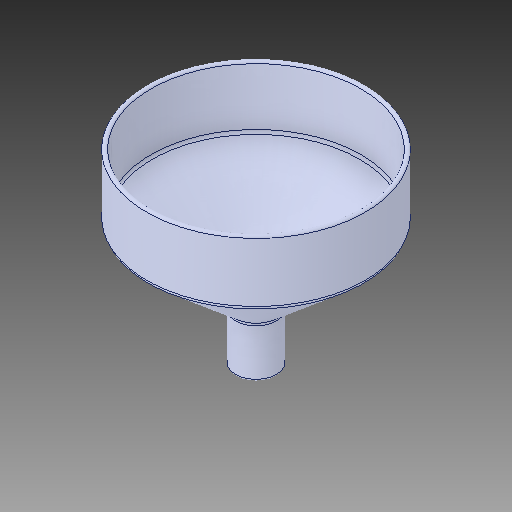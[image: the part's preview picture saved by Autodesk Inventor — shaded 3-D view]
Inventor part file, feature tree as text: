
AUTODESK INVENTOR PART (.ipt)
format: ipt  version: 2018 (Build 220112000, 112)  size: 160,256 bytes
history: native  units: in
note: dims shown in document units (in); Inventor stores cm internally (conversion verified against a paired STEP export)
features: fillet x1
ambient origin geometry x8: Origin, YZ Plane, XZ Plane, XY Plane, X Axis, Y Axis, Z Axis, Center Point
bodies: Solid1 (feature_tree)
feature tree (1):
  fillet  "Fillet10"  [1 undecoded]
note: 1 required parameter value undecoded (feature->parameter linkage not recoverable at this tier; creation-order binding heuristic only, values carry confidence <= 0.55)
